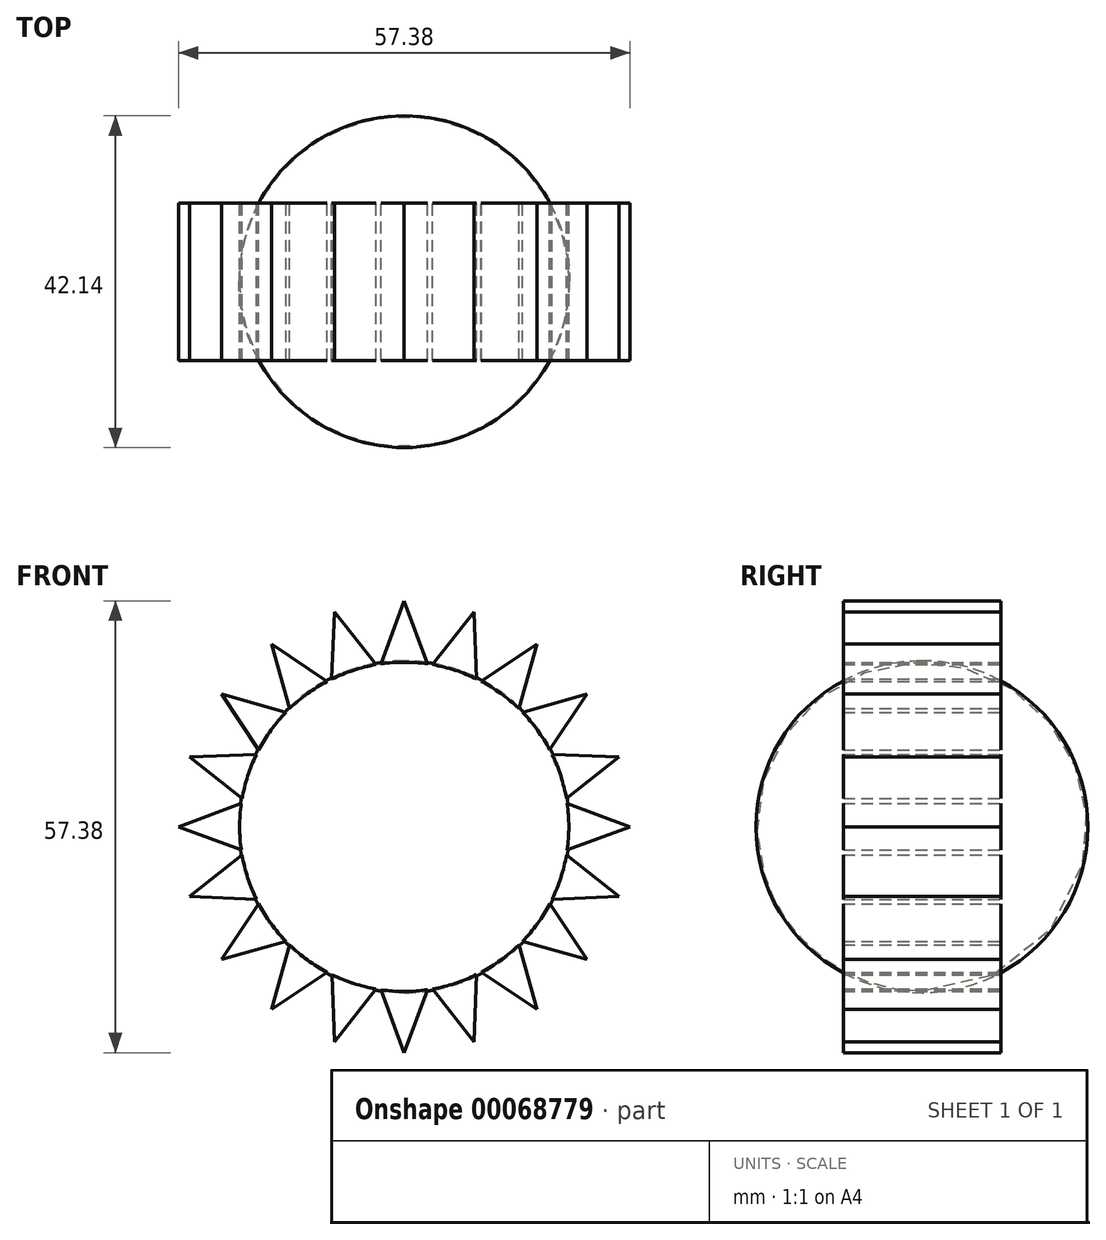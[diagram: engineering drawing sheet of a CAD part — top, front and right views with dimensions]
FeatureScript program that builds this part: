
annotation { "Feature Type Name" : "Feature", "Feature Type Description" : "" }
export const myFeature = defineFeature(function(context is Context, id is Id, definition is map)
    precondition{}
    {
        {
            var Q0;
            Q0=qCreatedBy(makeId("Front.planeOp"),FACE);
            var sketch = newSketch(context, id + "F0", { "sketchPlane" : qUnion([Q0])});
            skLineSegment(sketch, "E0", {"start": v(-21, 0) * mm, "end": v(21, 0) * mm});
            skArc(sketch, "E1", {"start": v(21, 0) * mm, "mid": v(0, 20.9) * mm, "end": v(-21, 0) * mm});
            skLineSegment(sketch, "E2", {"start": v(0, -0.08) * mm, "end": v(0, 20.9) * mm, "construction": true});
            skLineSegment(sketch, "E3", {"start": v(-2.96, 20.7) * mm, "end": v(0, 28.7) * mm});
            skLineSegment(sketch, "E4", {"start": v(0, 28.7) * mm, "end": v(2.94, 20.7) * mm});
            skSolve(sketch);
        }
        {
            var Q0;
            Q0=makeQuery(id+"F0.imprint","IMPRINT",FACE,{"disambiguationData":[TD([[makeQuery(id+"F0.imprint","IMPRINT",EDGE,{"derivedFrom":sQuery(id+"F0.wireOp",EDGE,"E0")}),1.0]])]});
            var Q1;
            Q1=sQuery(id+"F0.wireOp",EDGE,"E0");
            revolve(context, id + "F1", {"entities" : qUnion([Q0]), "axis" : qUnion([Q1]), "revolveType" : RevolveType.FULL});
        }
        {
            var Q0;
            {var subQ0=sQuery(id+"F0.wireOp",EDGE,"E3");Q0=makeQuery(id+"F0.imprint","IMPRINT",FACE,{"disambiguationData":[TD([[makeQuery(id+"F0.imprint","IMPRINT",EDGE,{"derivedFrom":subQ0}),-1.0]])]});}
            extrude(context, id + "F2", {"entities" : qUnion([Q0]), "depth" : 10 * mm, "hasSecondDirection" : true, "secondDirectionOppositeDirection" : true, "secondDirectionDepth" : 10 * mm});
        }
        {
            var Q0;
            Q0=qCreatedBy(makeId("Top.planeOp"),FACE);
            var sketch = newSketch(context, id + "F3", { "sketchPlane" : qUnion([Q0])});
            skLineSegment(sketch, "E5", {"start": v(0, -22.83) * mm, "end": v(0, 22.89) * mm, "construction": true});
            skSolve(sketch);
        }
        {
            var Q0;
            Q0=makeQuery(id+"F2.opExtrude","SWEPT_BODY",BODY,{"disambiguationData":[OSD([sQuery(id+"F0.wireOp",EDGE,"E1"),sQuery(id+"F0.wireOp",EDGE,"E3"),sQuery(id+"F0.wireOp",EDGE,"E4")])]});
            var Q1;
            Q1=sQuery(id+"F3.wireOp",EDGE,"E5");
            circularPattern(context, id + "F4", {"entities" : qUnion([Q0]), "axis" : qUnion([Q1]), "angle" : 360 * degree, "instanceCount" : 20, "equalSpace" : true});
        }
    });
